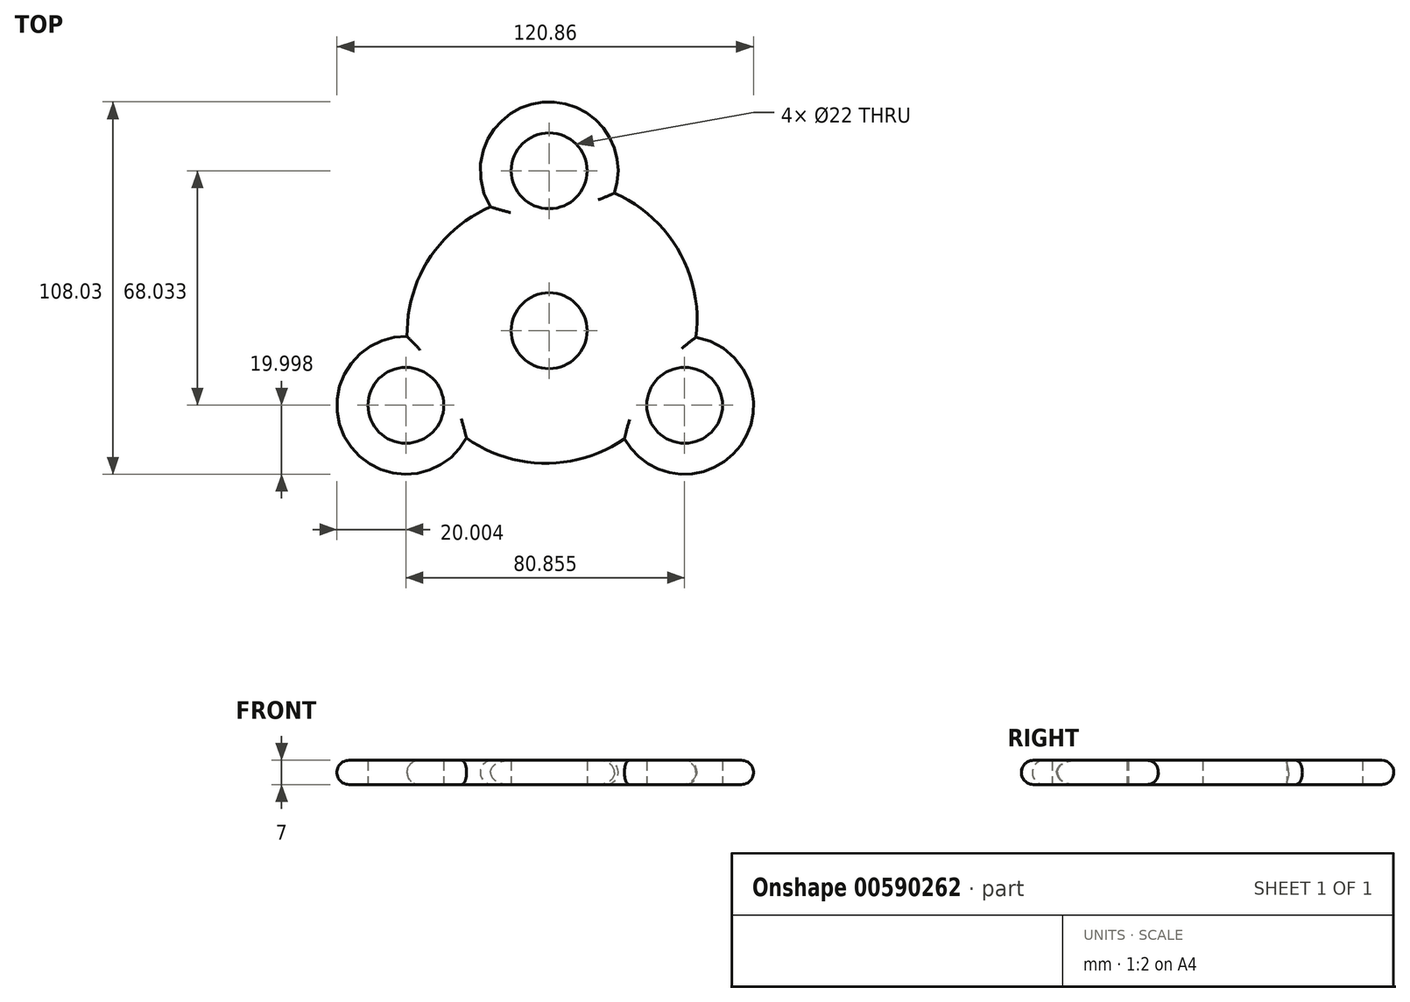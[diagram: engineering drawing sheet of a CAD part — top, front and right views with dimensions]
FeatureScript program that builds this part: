
annotation { "Feature Type Name" : "Feature", "Feature Type Description" : "" }
export const myFeature = defineFeature(function(context is Context, id is Id, definition is map)
    precondition{}
    {
        {
            var Q0;
            Q0=qCreatedBy(makeId("Top.planeOp"),FACE);
            var sketch = newSketch(context, id + "F0", { "sketchPlane" : qUnion([Q0])});
            skCircle(sketch, "E0", {"center": v(0, 0) * mm, "radius": 11 * mm});
            skPoint(sketch, "E1.center", {"position": v(0, -0.3) * mm});
            skArc(sketch, "E2", {"start": v(0, 0) * mm, "mid": v(-0.16, -0.52) * mm, "end": v(-0.31, -1.05) * mm});
            skArc(sketch, "E3", {"start": v(18.91, 39.9) * mm, "mid": v(-2.2, 66.27) * mm, "end": v(-17.03, 35.9) * mm});
            skArc(sketch, "E4", {"start": v(-41.23, -1.64) * mm, "mid": v(-58.85, -31.73) * mm, "end": v(-24, -31.17) * mm});
            skArc(sketch, "E5", {"start": v(21.82, -31.4) * mm, "mid": v(55.63, -33.16) * mm, "end": v(42.58, -1.92) * mm});
            skArc(sketch, "E6", {"start": v(18.91, 39.9) * mm, "mid": v(37.73, 22.94) * mm, "end": v(42.58, -1.92) * mm});
            skArc(sketch, "E7", {"start": v(21.82, -31.4) * mm, "mid": v(-1.12, -38.46) * mm, "end": v(-24, -31.17) * mm});
            skArc(sketch, "E8", {"start": v(-41.23, -1.64) * mm, "mid": v(-34.85, 20.82) * mm, "end": v(-17.03, 35.9) * mm});
            skPoint(sketch, "E9.start.orphan", {"position": v(-30.58, -27.6) * mm});
            skCircle(sketch, "E10", {"center": v(-41.58, -21.64) * mm, "radius": 11 * mm});
            skCircle(sketch, "E11", {"center": v(39.28, -21.64) * mm, "radius": 11 * mm});
            skCircle(sketch, "E12", {"center": v(0, 46.4) * mm, "radius": 11 * mm});
            skSolve(sketch);
        }
        {
            var Q0;
            Q0 = qSketchRegion(id + "F0", true);
            extrude(context, id + "F1", {"entities" : qUnion([Q0]), "depth" : 7 * mm, "offsetDistance" : 25 * mm});
        }
        {
            var Q0;
            Q0=makeQuery(id+"F1.opExtrude","CAP_EDGE",EDGE,{"disambiguationData":[OSD([sQuery(id+"F0.wireOp",EDGE,"E5")])],"isStart":false});
            var Q1;
            Q1=makeQuery(id+"F1.opExtrude","CAP_EDGE",EDGE,{"disambiguationData":[OSD([sQuery(id+"F0.wireOp",EDGE,"E7")])],"isStart":false});
            var Q2;
            Q2=makeQuery(id+"F1.opExtrude","CAP_EDGE",EDGE,{"disambiguationData":[OSD([sQuery(id+"F0.wireOp",EDGE,"E4")])],"isStart":false});
            var Q3;
            Q3=makeQuery(id+"F1.opExtrude","CAP_EDGE",EDGE,{"disambiguationData":[OSD([sQuery(id+"F0.wireOp",EDGE,"E8")])],"isStart":false});
            var Q4;
            Q4=makeQuery(id+"F1.opExtrude","CAP_EDGE",EDGE,{"disambiguationData":[OSD([sQuery(id+"F0.wireOp",EDGE,"E3")])],"isStart":false});
            var Q5;
            Q5=makeQuery(id+"F1.opExtrude","CAP_EDGE",EDGE,{"disambiguationData":[OSD([sQuery(id+"F0.wireOp",EDGE,"E6")])],"isStart":false});
            var Q6;
            Q6=makeQuery(id+"F1.opExtrude","CAP_EDGE",EDGE,{"disambiguationData":[OSD([sQuery(id+"F0.wireOp",EDGE,"E6")])],"isStart":true});
            var Q7;
            Q7=makeQuery(id+"F1.opExtrude","CAP_EDGE",EDGE,{"disambiguationData":[OSD([sQuery(id+"F0.wireOp",EDGE,"E5")])],"isStart":true});
            var Q8;
            Q8=makeQuery(id+"F1.opExtrude","CAP_EDGE",EDGE,{"disambiguationData":[OSD([sQuery(id+"F0.wireOp",EDGE,"E7")])],"isStart":true});
            var Q9;
            Q9=makeQuery(id+"F1.opExtrude","CAP_EDGE",EDGE,{"disambiguationData":[OSD([sQuery(id+"F0.wireOp",EDGE,"E4")])],"isStart":true});
            var Q10;
            Q10=makeQuery(id+"F1.opExtrude","CAP_EDGE",EDGE,{"disambiguationData":[OSD([sQuery(id+"F0.wireOp",EDGE,"E8")])],"isStart":true});
            var Q11;
            Q11=makeQuery(id+"F1.opExtrude","CAP_EDGE",EDGE,{"disambiguationData":[OSD([sQuery(id+"F0.wireOp",EDGE,"E3")])],"isStart":true});
            fillet(context, id + "F2", {"entities" : qUnion([Q0, Q1, Q2, Q3, Q4, Q5, Q6, Q7, Q8, Q9, Q10, Q11]), "radius" : 3.5 * mm, "tangentPropagation" : true, "allowEdgeOverflow" : false});
        }
    });
